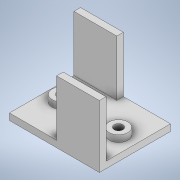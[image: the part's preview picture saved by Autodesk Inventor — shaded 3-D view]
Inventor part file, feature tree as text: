
AUTODESK INVENTOR PART (.ipt)
format: ipt  version: 2020 (Build 240168000, 168)  size: 169,472 bytes
history: native  units: in
note: dims shown in document units (in); Inventor stores cm internally (conversion verified against a paired STEP export)
features: extrude x7, sketch x7
ambient origin geometry x8: Origin, YZ Plane, XZ Plane, XY Plane, X Axis, Y Axis, Z Axis, Center Point
bodies: Solid1 (feature_tree)
feature tree (14):
  extrude  "Extrusion1"  Depth=1.2756in
  extrude  "Extrusion3"  Depth=0.1181in
  extrude  "Extrusion4"  Depth=1.0in TaperAngle=0.0deg
  extrude  "Extrusion5"  Depth=0.1181in TaperAngle=0.0deg
  extrude  "Extrusion6"  Depth=0.1181in TaperAngle=0.0deg
  extrude  "Extrusion7"  Depth=0.3346in
  extrude  "Extrusion8"  Depth=0.1181in
  sketch  "Sketch1"  dims[d0=1.6142in d1=1.2756in]
  sketch  "Sketch3"  dims[d2=0.1181in d3=0.0in d8=0.1181in]
  sketch  "Sketch4"  dims[d9=0.1181in d10=1.0in d11=0.0in]
  sketch  "Sketch5"  dims[d12=0.8465in d13=0.1181in d14=0.0in]
  sketch  "Sketch6"  dims[d15=0.8465in d16=0.1181in d17=0.0in]
  sketch  "Sketch7"  dims[d20=0.3346in d21=0.3346in]
  sketch  "Sketch8"  dims[d22=0.1181in d23=0.0in d24=0.1575in d25=0.1575in d26=0.2362in d27=0.0in d28=0.2362in d29=0.2362in d30=0.1181in d31=0.0in d32=1.0236in d33=0.2953in d34=0.2953in]
